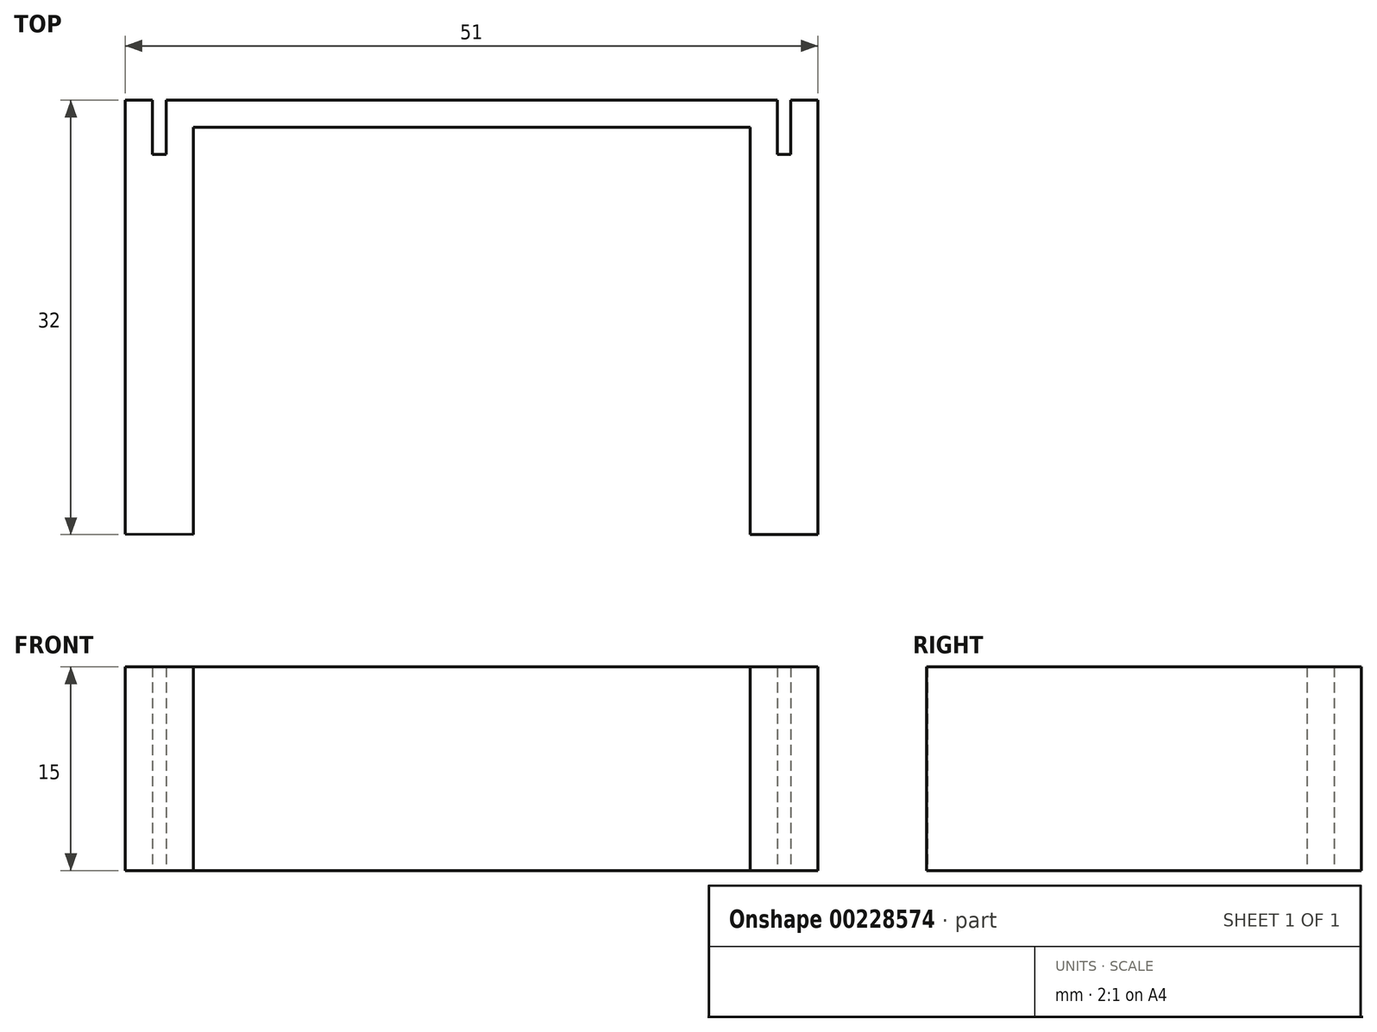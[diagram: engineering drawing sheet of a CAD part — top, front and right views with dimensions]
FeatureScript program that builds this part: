
annotation { "Feature Type Name" : "Feature", "Feature Type Description" : "" }
export const myFeature = defineFeature(function(context is Context, id is Id, definition is map)
    precondition{}
    {
        {
            var Q0;
            Q0=qCreatedBy(makeId("Top.planeOp"),FACE);
            var sketch = newSketch(context, id + "F0", { "sketchPlane" : qUnion([Q0])});
            skLineSegment(sketch, "E0", {"start": v(-21.23, -3.72) * mm, "end": v(19.77, -3.72) * mm});
            skLineSegment(sketch, "E1", {"start": v(-21.23, -3.72) * mm, "end": v(-21.23, -33.72) * mm});
            skLineSegment(sketch, "E2", {"start": v(19.77, -3.72) * mm, "end": v(19.77, -33.72) * mm});
            skLineSegment(sketch, "E3.0", {"start": v(-26.23, -1.72) * mm, "end": v(-26.23, -33.68) * mm});
            skLineSegment(sketch, "E3.2", {"start": v(24.77, -1.72) * mm, "end": v(24.77, -33.72) * mm});
            skLineSegment(sketch, "E4", {"start": v(19.77, -33.72) * mm, "end": v(24.77, -33.72) * mm});
            skLineSegment(sketch, "E5", {"start": v(-21.23, -33.72) * mm, "end": v(-26.23, -33.68) * mm});
            skLineSegment(sketch, "E6", {"start": v(-0.73, -1.72) * mm, "end": v(-0.73, 12.19) * mm, "construction": true});
            skLineSegment(sketch, "E7", {"start": v(-24.23, -1.72) * mm, "end": v(-24.23, -5.72) * mm});
            skLineSegment(sketch, "E8", {"start": v(-24.23, -5.72) * mm, "end": v(-23.23, -5.72) * mm});
            skLineSegment(sketch, "E9", {"start": v(-23.23, -5.72) * mm, "end": v(-23.23, -1.72) * mm});
            skLineSegment(sketch, "E10", {"start": v(-26.23, -1.72) * mm, "end": v(-24.23, -1.72) * mm});
            skLineSegment(sketch, "E11.MirrorCS", {"start": v(21.77, -5.72) * mm, "end": v(21.77, -1.72) * mm});
            skLineSegment(sketch, "E12.MirrorCS", {"start": v(22.77, -5.72) * mm, "end": v(21.77, -5.72) * mm});
            skLineSegment(sketch, "E13.MirrorCS", {"start": v(24.77, -1.72) * mm, "end": v(22.77, -1.72) * mm});
            skLineSegment(sketch, "E14.MirrorCS", {"start": v(22.77, -1.72) * mm, "end": v(22.77, -5.72) * mm});
            skLineSegment(sketch, "E15", {"start": v(-23.23, -1.72) * mm, "end": v(21.77, -1.72) * mm});
            skSolve(sketch);
        }
        {
            var Q0;
            Q0=makeQuery(id+"F0.imprint","IMPRINT",FACE,{"disambiguationData":[TD([[makeQuery(id+"F0.imprint","IMPRINT",EDGE,{"derivedFrom":sQuery(id+"F0.wireOp",EDGE,"E0")}),1.0]])]});
            var Q1;
            Q1=makeQuery(id+"F0.imprint","IMPRINT",FACE,{"disambiguationData":[TD([[makeQuery(id+"F0.imprint","IMPRINT",EDGE,{"derivedFrom":sQuery(id+"F0.wireOp",EDGE,"c177bd56-2118-4478-aafe-a5c0906669d23.MirrorCS")}),-1.0]])]});
            var Q2;
            Q2=makeQuery(id+"F0.imprint","IMPRINT",FACE,{"disambiguationData":[TD([[makeQuery(id+"F0.imprint","IMPRINT",EDGE,{"derivedFrom":sQuery(id+"F0.wireOp",EDGE,"28c78ba8-1c2f-4a24-b17a-493018df2ab50.MirrorCS")}),-1.0]])]});
            var Q3;
            Q3=makeQuery(id+"F0.imprint","IMPRINT",FACE,{"disambiguationData":[TD([[makeQuery(id+"F0.imprint","IMPRINT",EDGE,{"derivedFrom":sQuery(id+"F0.wireOp",EDGE,"VMr5lGmS-ZMll-HL2w-axOE-yeSVmUCzqS3u.bottom")}),1.0]])]});
            var Q4;
            Q4=makeQuery(id+"F0.imprint","IMPRINT",FACE,{"disambiguationData":[TD([[makeQuery(id+"F0.imprint","IMPRINT",EDGE,{"derivedFrom":sQuery(id+"F0.wireOp",EDGE,"c177bd56-2118-4478-aafe-a5c0906669d20.MirrorCS")}),-1.0]])]});
            extrude(context, id + "F1", {"entities" : qUnion([Q0, Q1, Q2, Q3, Q4]), "depth" : 15 * mm});
        }
    });
